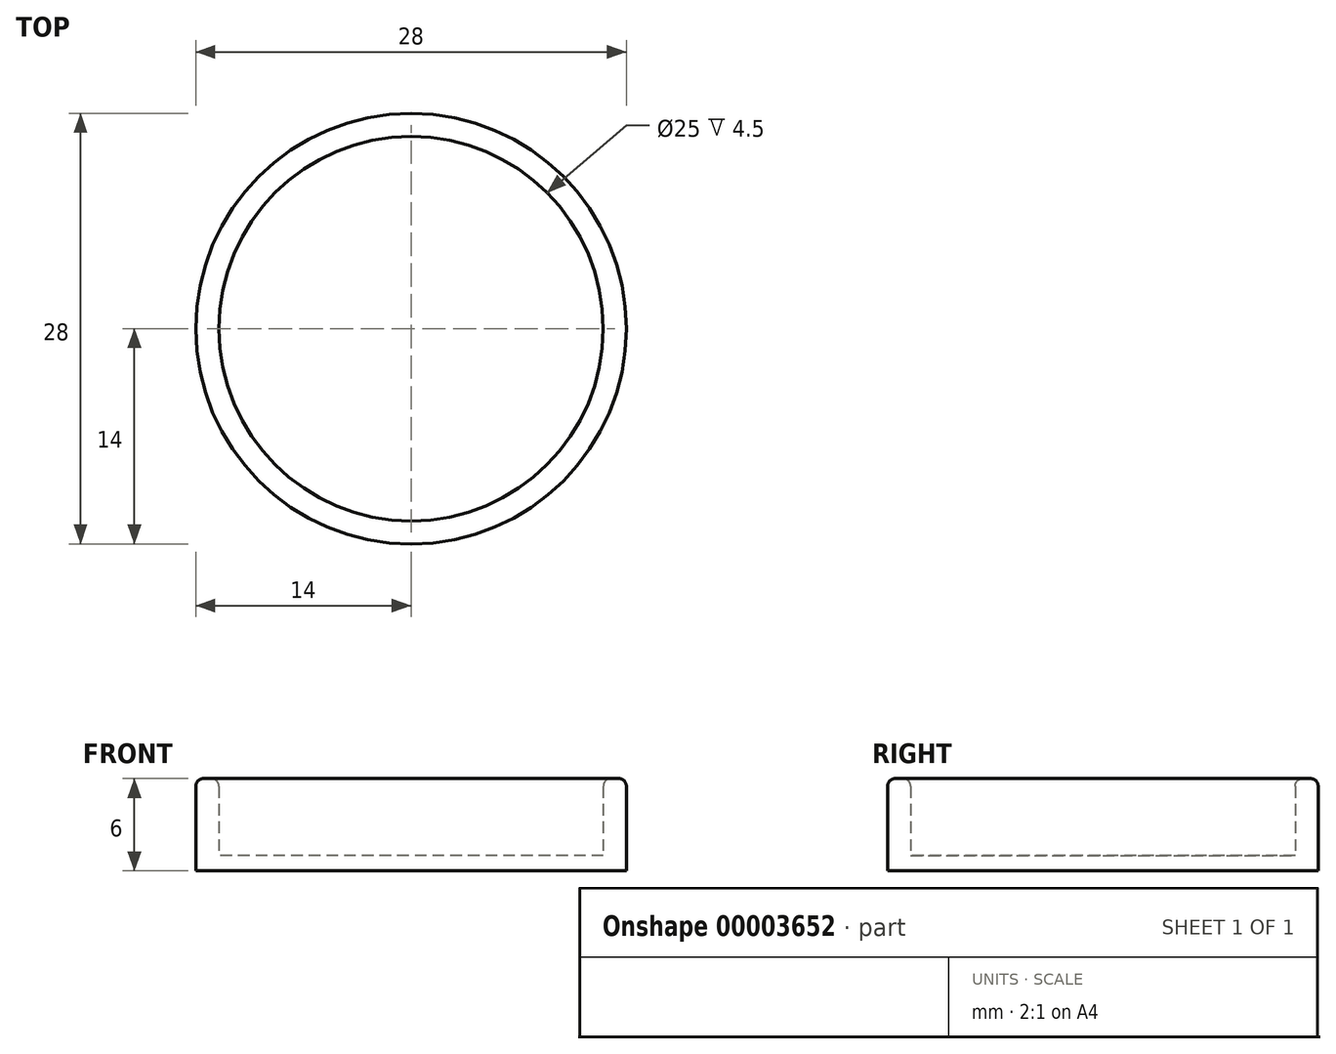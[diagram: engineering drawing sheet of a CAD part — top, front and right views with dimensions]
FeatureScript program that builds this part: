
annotation { "Feature Type Name" : "Feature", "Feature Type Description" : "" }
export const myFeature = defineFeature(function(context is Context, id is Id, definition is map)
    precondition{}
    {
        {
            var Q0;
            Q0=qCreatedBy(makeId("Top.planeOp"),FACE);
            var sketch = newSketch(context, id + "F0", { "sketchPlane" : qUnion([Q0])});
            skCircle(sketch, "E0", {"center": v(0, 0) * mm, "radius": 12.5 * mm});
            skCircle(sketch, "E1", {"center": v(0, 0) * mm, "radius": 14 * mm});
            skSolve(sketch);
        }
        {
            var Q0;
            Q0=makeQuery(id+"F0.imprint","IMPRINT",FACE,{"disambiguationData":[TD([[makeQuery(id+"F0.imprint","IMPRINT",EDGE,{"derivedFrom":sQuery(id+"F0.wireOp",EDGE,"E0")}),1.0]])]});
            extrude(context, id + "F1", {"entities" : qUnion([Q0]), "depth" : 1 * mm});
        }
        {
            var Q0;
            Q0=makeQuery(id+"F0.imprint","IMPRINT",FACE,{"disambiguationData":[TD([[makeQuery(id+"F0.imprint","IMPRINT",EDGE,{"derivedFrom":sQuery(id+"F0.wireOp",EDGE,"E0")}),-1.0]])]});
            extrude(context, id + "F2", {"entities" : qUnion([Q0]), "operationType" : NewBodyOperationType.ADD, "depth" : 6 * mm});
        }
        {
            var Q0;
            Q0=makeQuery(id+"F2.opExtrude","CAP_FACE",FACE,{"disambiguationData":[OSD([sQuery(id+"F0.wireOp",EDGE,"E0"),sQuery(id+"F0.wireOp",EDGE,"E1")])],"isStart":false});
            fillet(context, id + "F3", {"entities" : qUnion([Q0]), "radius" : 0.5 * mm, "tangentPropagation" : true, "allowEdgeOverflow" : false});
        }
    });
